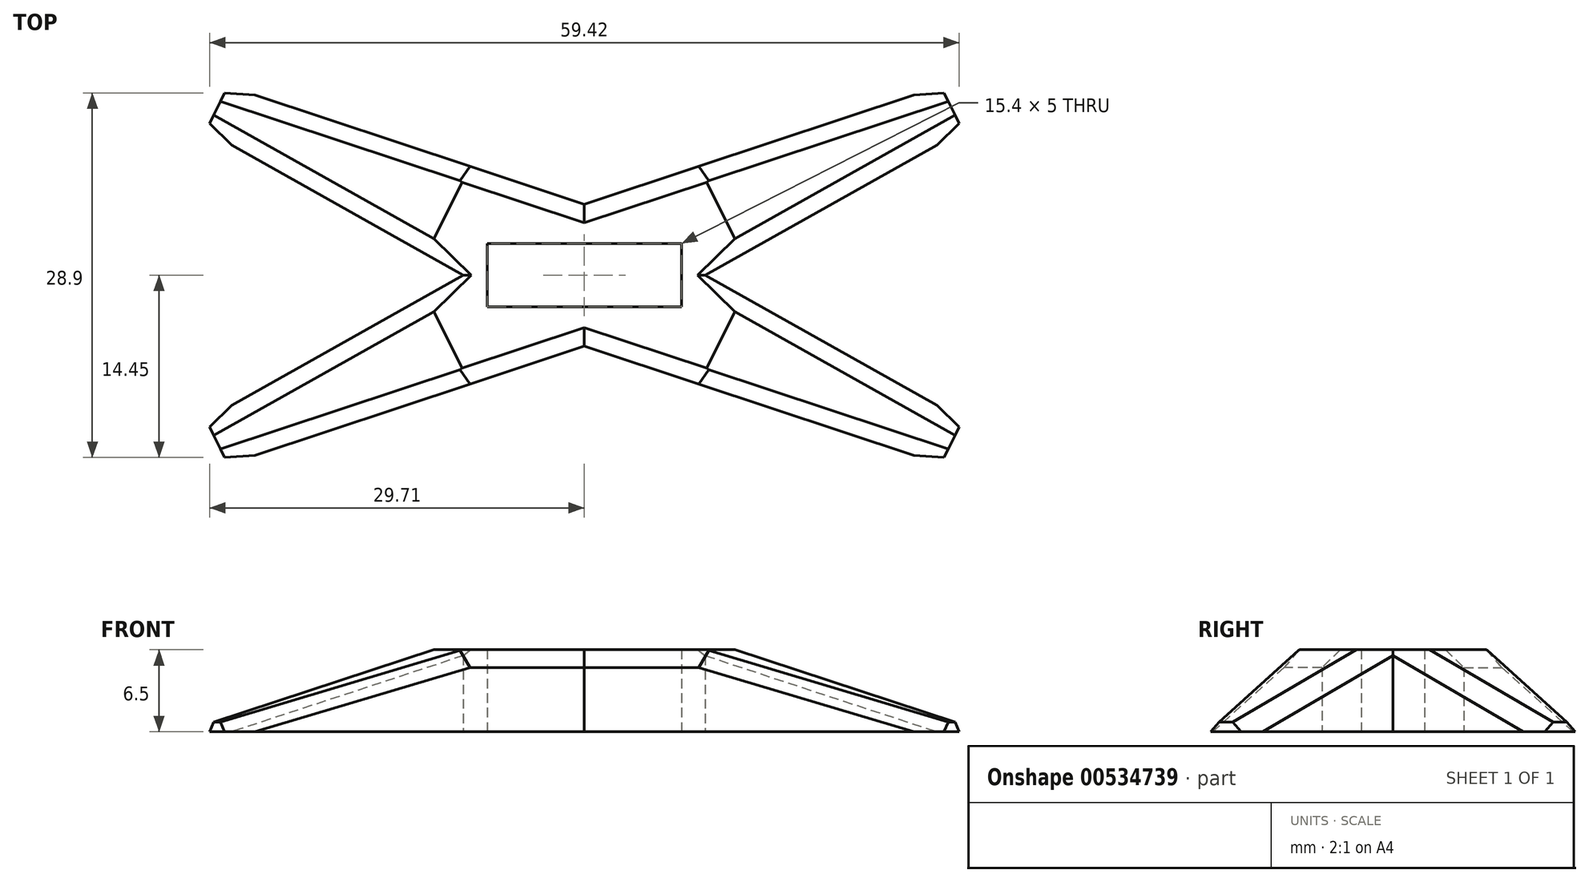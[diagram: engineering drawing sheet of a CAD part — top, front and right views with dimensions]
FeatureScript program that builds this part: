
annotation { "Feature Type Name" : "Feature", "Feature Type Description" : "" }
export const myFeature = defineFeature(function(context is Context, id is Id, definition is map)
    precondition{}
    {
        {
            var Q0;
            Q0=qCreatedBy(makeId("Top.planeOp"),FACE);
            var sketch = newSketch(context, id + "F0", { "sketchPlane" : qUnion([Q0])});
            skLineSegment(sketch, "E0.bottom", {"start": v(7.7, -2.5) * mm, "end": v(-7.7, -2.5) * mm});
            skLineSegment(sketch, "E0.top", {"start": v(7.7, 2.5) * mm, "end": v(-7.7, 2.5) * mm});
            skLineSegment(sketch, "E0.left", {"start": v(7.7, -2.5) * mm, "end": v(7.7, 2.5) * mm});
            skLineSegment(sketch, "E0.right", {"start": v(-7.7, -2.5) * mm, "end": v(-7.7, 2.5) * mm});
            skPoint(sketch, "E0.middle", {"position": v(0, 0) * mm});
            skLineSegment(sketch, "E1.bottom", {"start": v(30, -15) * mm, "end": v(-30, -15) * mm, "construction": true});
            skLineSegment(sketch, "E1.top", {"start": v(30, 15) * mm, "end": v(-30, 15) * mm, "construction": true});
            skLineSegment(sketch, "E1.left", {"start": v(30, -15) * mm, "end": v(30, 15) * mm, "construction": true});
            skLineSegment(sketch, "E1.right", {"start": v(-30, -15) * mm, "end": v(-30, 15) * mm, "construction": true});
            skLineSegment(sketch, "E2", {"start": v(9.59, 0) * mm, "end": v(30, 11.47) * mm});
            skLineSegment(sketch, "E3", {"start": v(30, 11.47) * mm, "end": v(28.23, 15) * mm});
            skLineSegment(sketch, "E4", {"start": v(28.23, 15) * mm, "end": v(0, 5.63) * mm});
            skLineSegment(sketch, "E5", {"start": v(0, 5.63) * mm, "end": v(-28.23, 15) * mm});
            skLineSegment(sketch, "E6", {"start": v(-28.23, 15) * mm, "end": v(-30, 11.47) * mm});
            skLineSegment(sketch, "E7", {"start": v(-30, 11.47) * mm, "end": v(-9.59, 0) * mm});
            skLineSegment(sketch, "E8", {"start": v(-9.59, 0) * mm, "end": v(-30, -11.47) * mm});
            skLineSegment(sketch, "E9", {"start": v(-30, -11.47) * mm, "end": v(-28.23, -15) * mm});
            skLineSegment(sketch, "E10", {"start": v(-28.23, -15) * mm, "end": v(0, -5.63) * mm});
            skLineSegment(sketch, "E11", {"start": v(0, -5.63) * mm, "end": v(28.23, -15) * mm});
            skLineSegment(sketch, "E12", {"start": v(28.23, -15) * mm, "end": v(30, -11.47) * mm});
            skLineSegment(sketch, "E13", {"start": v(30, -11.47) * mm, "end": v(9.59, 0) * mm});
            skLineSegment(sketch, "E14", {"start": v(-30, 15) * mm, "end": v(30, -15) * mm, "construction": true});
            skSolve(sketch);
        }
        {
            var Q0;
            Q0=makeQuery(id+"F0.imprint","IMPRINT",FACE,{"disambiguationData":[TD([[makeQuery(id+"F0.imprint","IMPRINT",EDGE,{"derivedFrom":sQuery(id+"F0.wireOp",EDGE,"E0.bottom")}),1.0]])]});
            extrude(context, id + "F1", {"entities" : qUnion([Q0]), "depth" : 6.5 * mm, "offsetDistance" : 25 * mm});
        }
        {
            var Q0;
            Q0=makeQuery(id+"F1.opExtrude","CAP_EDGE",EDGE,{"disambiguationData":[OSD([sQuery(id+"F0.wireOp",EDGE,"E3")])],"isStart":false});
            var Q1;
            Q1=makeQuery(id+"F1.opExtrude","CAP_EDGE",EDGE,{"disambiguationData":[OSD([sQuery(id+"F0.wireOp",EDGE,"E12")])],"isStart":false});
            var Q2;
            Q2=makeQuery(id+"F1.opExtrude","CAP_EDGE",EDGE,{"disambiguationData":[OSD([sQuery(id+"F0.wireOp",EDGE,"E9")])],"isStart":false});
            var Q3;
            Q3=makeQuery(id+"F1.opExtrude","CAP_EDGE",EDGE,{"disambiguationData":[OSD([sQuery(id+"F0.wireOp",EDGE,"E6")])],"isStart":false});
            chamfer(context, id + "F2", {"entities" : qUnion([Q0, Q1, Q2, Q3]), "chamferType" : ChamferType.OFFSET_ANGLE, "width" : 20 * mm, "oppositeDirection" : false, "angle" : 16 * degree, "tangentPropagation" : true});
        }
        {
            var Q0;
            Q0=makeQuery(id+"F2.opChamfer","BLEND_EDGE",EDGE,{"blendedFrom":[makeQuery(id+"F1.opExtrude","CAP_EDGE",EDGE,{"disambiguationData":[OSD([sQuery(id+"F0.wireOp",EDGE,"E9")])],"isStart":false}),makeQuery(id+"F1.opExtrude","SWEPT_FACE",FACE,{"disambiguationData":[OSD([sQuery(id+"F0.wireOp",EDGE,"E10")])]})],"blendedInto":[makeQuery(id+"F1.opExtrude","SWEPT_FACE",FACE,{"disambiguationData":[OSD([sQuery(id+"F0.wireOp",EDGE,"E10")])]})]});
            var Q1;
            Q1=makeQuery(id+"F2.opChamfer","BLEND_EDGE",EDGE,{"blendedFrom":[makeQuery(id+"F1.opExtrude","CAP_EDGE",EDGE,{"disambiguationData":[OSD([sQuery(id+"F0.wireOp",EDGE,"E9")])],"isStart":false}),makeQuery(id+"F1.opExtrude","SWEPT_FACE",FACE,{"disambiguationData":[OSD([sQuery(id+"F0.wireOp",EDGE,"E8")])]})],"blendedInto":[makeQuery(id+"F1.opExtrude","SWEPT_FACE",FACE,{"disambiguationData":[OSD([sQuery(id+"F0.wireOp",EDGE,"E8")])]})]});
            var Q2;
            Q2=makeQuery(id+"F2.opChamfer","BLEND_EDGE",EDGE,{"blendedFrom":[makeQuery(id+"F1.opExtrude","CAP_EDGE",EDGE,{"disambiguationData":[OSD([sQuery(id+"F0.wireOp",EDGE,"E6")])],"isStart":false}),makeQuery(id+"F1.opExtrude","SWEPT_FACE",FACE,{"disambiguationData":[OSD([sQuery(id+"F0.wireOp",EDGE,"E7")])]})],"blendedInto":[makeQuery(id+"F1.opExtrude","SWEPT_FACE",FACE,{"disambiguationData":[OSD([sQuery(id+"F0.wireOp",EDGE,"E7")])]})]});
            var Q3;
            Q3=makeQuery(id+"F2.opChamfer","BLEND_EDGE",EDGE,{"blendedFrom":[makeQuery(id+"F1.opExtrude","CAP_EDGE",EDGE,{"disambiguationData":[OSD([sQuery(id+"F0.wireOp",EDGE,"E6")])],"isStart":false}),makeQuery(id+"F1.opExtrude","SWEPT_FACE",FACE,{"disambiguationData":[OSD([sQuery(id+"F0.wireOp",EDGE,"E5")])]})],"blendedInto":[makeQuery(id+"F1.opExtrude","SWEPT_FACE",FACE,{"disambiguationData":[OSD([sQuery(id+"F0.wireOp",EDGE,"E5")])]})]});
            var Q4;
            Q4=makeQuery(id+"F2.opChamfer","BLEND_EDGE",EDGE,{"blendedFrom":[makeQuery(id+"F1.opExtrude","CAP_EDGE",EDGE,{"disambiguationData":[OSD([sQuery(id+"F0.wireOp",EDGE,"E3")])],"isStart":false}),makeQuery(id+"F1.opExtrude","SWEPT_FACE",FACE,{"disambiguationData":[OSD([sQuery(id+"F0.wireOp",EDGE,"E4")])]})],"blendedInto":[makeQuery(id+"F1.opExtrude","SWEPT_FACE",FACE,{"disambiguationData":[OSD([sQuery(id+"F0.wireOp",EDGE,"E4")])]})]});
            var Q5;
            Q5=makeQuery(id+"F2.opChamfer","BLEND_EDGE",EDGE,{"blendedFrom":[makeQuery(id+"F1.opExtrude","CAP_EDGE",EDGE,{"disambiguationData":[OSD([sQuery(id+"F0.wireOp",EDGE,"E3")])],"isStart":false}),makeQuery(id+"F1.opExtrude","SWEPT_FACE",FACE,{"disambiguationData":[OSD([sQuery(id+"F0.wireOp",EDGE,"E2")])]})],"blendedInto":[makeQuery(id+"F1.opExtrude","SWEPT_FACE",FACE,{"disambiguationData":[OSD([sQuery(id+"F0.wireOp",EDGE,"E2")])]})]});
            var Q6;
            Q6=makeQuery(id+"F2.opChamfer","BLEND_EDGE",EDGE,{"blendedFrom":[makeQuery(id+"F1.opExtrude","CAP_EDGE",EDGE,{"disambiguationData":[OSD([sQuery(id+"F0.wireOp",EDGE,"E12")])],"isStart":false}),makeQuery(id+"F1.opExtrude","SWEPT_FACE",FACE,{"disambiguationData":[OSD([sQuery(id+"F0.wireOp",EDGE,"E13")])]})],"blendedInto":[makeQuery(id+"F1.opExtrude","SWEPT_FACE",FACE,{"disambiguationData":[OSD([sQuery(id+"F0.wireOp",EDGE,"E13")])]})]});
            var Q7;
            Q7=makeQuery(id+"F2.opChamfer","BLEND_EDGE",EDGE,{"blendedFrom":[makeQuery(id+"F1.opExtrude","CAP_EDGE",EDGE,{"disambiguationData":[OSD([sQuery(id+"F0.wireOp",EDGE,"E12")])],"isStart":false}),makeQuery(id+"F1.opExtrude","SWEPT_FACE",FACE,{"disambiguationData":[OSD([sQuery(id+"F0.wireOp",EDGE,"E11")])]})],"blendedInto":[makeQuery(id+"F1.opExtrude","SWEPT_FACE",FACE,{"disambiguationData":[OSD([sQuery(id+"F0.wireOp",EDGE,"E11")])]})]});
            var Q8;
            Q8=makeQuery(id+"F1.opExtrude","CAP_EDGE",EDGE,{"disambiguationData":[OSD([sQuery(id+"F0.wireOp",EDGE,"E11")])],"isStart":false});
            var Q9;
            Q9=makeQuery(id+"F1.opExtrude","CAP_EDGE",EDGE,{"disambiguationData":[OSD([sQuery(id+"F0.wireOp",EDGE,"E10")])],"isStart":false});
            var Q10;
            Q10=makeQuery(id+"F1.opExtrude","CAP_EDGE",EDGE,{"disambiguationData":[OSD([sQuery(id+"F0.wireOp",EDGE,"E4")])],"isStart":false});
            var Q11;
            Q11=makeQuery(id+"F1.opExtrude","CAP_EDGE",EDGE,{"disambiguationData":[OSD([sQuery(id+"F0.wireOp",EDGE,"E5")])],"isStart":false});
            chamfer(context, id + "F3", {"entities" : qUnion([Q0, Q1, Q2, Q3, Q4, Q5, Q6, Q7, Q8, Q9, Q10, Q11]), "width" : 1.4 * mm, "tangentPropagation" : true});
        }
    });
